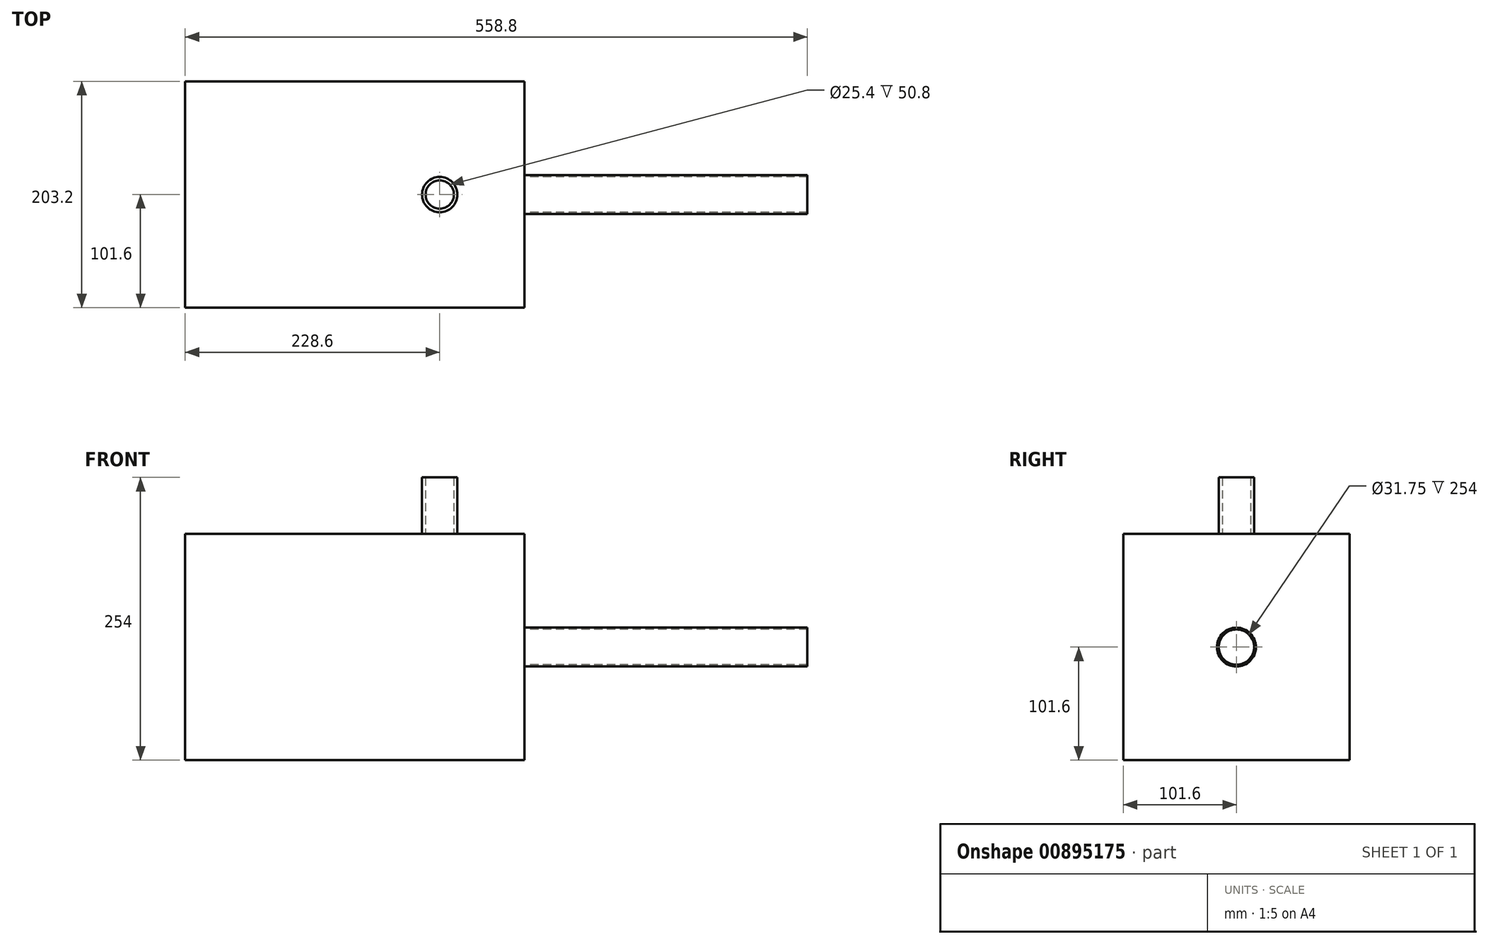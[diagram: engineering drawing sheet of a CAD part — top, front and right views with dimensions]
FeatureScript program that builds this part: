
annotation { "Feature Type Name" : "Feature", "Feature Type Description" : "" }
export const myFeature = defineFeature(function(context is Context, id is Id, definition is map)
    precondition{}
    {
        {
            var Q0;
            Q0=qCreatedBy(makeId("Front.planeOp"),FACE);
            var sketch = newSketch(context, id + "F0", { "sketchPlane" : qUnion([Q0])});
            skLineSegment(sketch, "E0.bottom", {"start": v(0, 0) * mm, "end": v(304.8, 0) * mm});
            skLineSegment(sketch, "E0.top", {"start": v(0, 203.2) * mm, "end": v(304.8, 203.2) * mm});
            skLineSegment(sketch, "E0.left", {"start": v(0, 0) * mm, "end": v(0, 203.2) * mm});
            skLineSegment(sketch, "E0.right", {"start": v(304.8, 0) * mm, "end": v(304.8, 203.2) * mm});
            skSolve(sketch);
        }
        {
            var Q0;
            Q0=qSketchRegion(id+"F0",true);
            extrude(context, id + "F1", {"entities" : qUnion([Q0]), "depth" : 203.2 * mm, "offsetDistance" : 25 * mm});
        }
        {
            var Q0;
            Q0=makeQuery(id+"F1.opExtrude","SWEPT_FACE",FACE,{"disambiguationData":[OSD([sQuery(id+"F0.wireOp",EDGE,"E0.right")])]});
            var sketch = newSketch(context, id + "F2", { "sketchPlane" : qUnion([Q0])});
            skLineSegment(sketch, "E1", {"start": v(-203.2, 203.2) * mm, "end": v(0, 0) * mm, "construction": true});
            skCircle(sketch, "E2", {"center": v(-101.6, 101.6) * mm, "radius": 15.88 * mm});
            skCircle(sketch, "E3", {"center": v(-101.6, 101.6) * mm, "radius": 17.46 * mm});
            skSolve(sketch);
        }
        {
            var Q0;
            Q0=qSketchRegion(id+"F2",true);
            extrude(context, id + "F3", {"entities" : qUnion([Q0]), "operationType" : NewBodyOperationType.ADD, "depth" : 254 * mm, "offsetDistance" : 25 * mm});
        }
        {
            var Q0;
            Q0=makeQuery(id+"F1.opExtrude","SWEPT_FACE",FACE,{"disambiguationData":[OSD([sQuery(id+"F0.wireOp",EDGE,"E0.top")])]});
            var sketch = newSketch(context, id + "F4", { "sketchPlane" : qUnion([Q0])});
            skLineSegment(sketch, "E4", {"start": v(304.8, -101.6) * mm, "end": v(0, -101.6) * mm, "construction": true});
            skCircle(sketch, "E5", {"center": v(228.6, -101.6) * mm, "radius": 12.7 * mm});
            skCircle(sketch, "E6", {"center": v(228.6, -101.6) * mm, "radius": 15.88 * mm});
            skSolve(sketch);
        }
        {
            var Q0;
            Q0=qSketchRegion(id+"F4",true);
            extrude(context, id + "F5", {"entities" : qUnion([Q0]), "operationType" : NewBodyOperationType.ADD, "depth" : 50.8 * mm, "offsetDistance" : 25 * mm});
        }
    });
